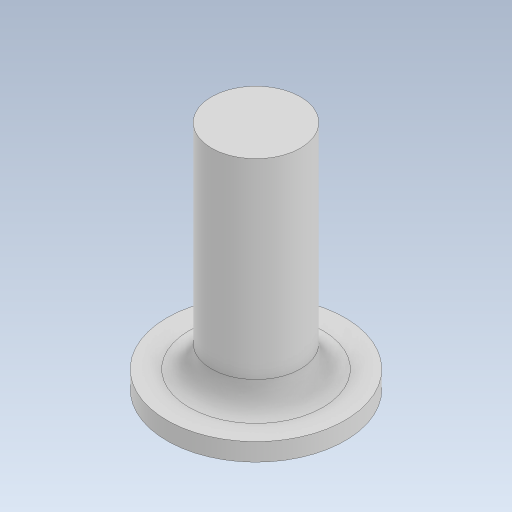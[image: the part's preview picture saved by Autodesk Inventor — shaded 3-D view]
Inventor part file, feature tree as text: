
AUTODESK INVENTOR PART (.ipt)
format: ipt  version: 2023 (Build 270158000, 158)  size: 293,888 bytes
history: native  units: in
note: dims shown in document units (in); Inventor stores cm internally (conversion verified against a paired STEP export)
features: extrude x2, sketch x1, fillet x1
ambient origin geometry x8: Origin, YZ Plane, XZ Plane, XY Plane, X Axis, Y Axis, Z Axis, Center Point
bodies: Solid1 (feature_tree)
feature tree (4):
  sketch  "Sketch1"  dims[d0=0.5in d1=0.25in d2=0.6in d3=0.0in d4=0.05in d5=0.0in d6=0.0625in]
  extrude  "Extrusion1"  Depth=0.25in
  extrude  "Extrusion2"  Depth=0.6in TaperAngle=0.0deg
  fillet  "Fillet1"  Radius=0.05in
